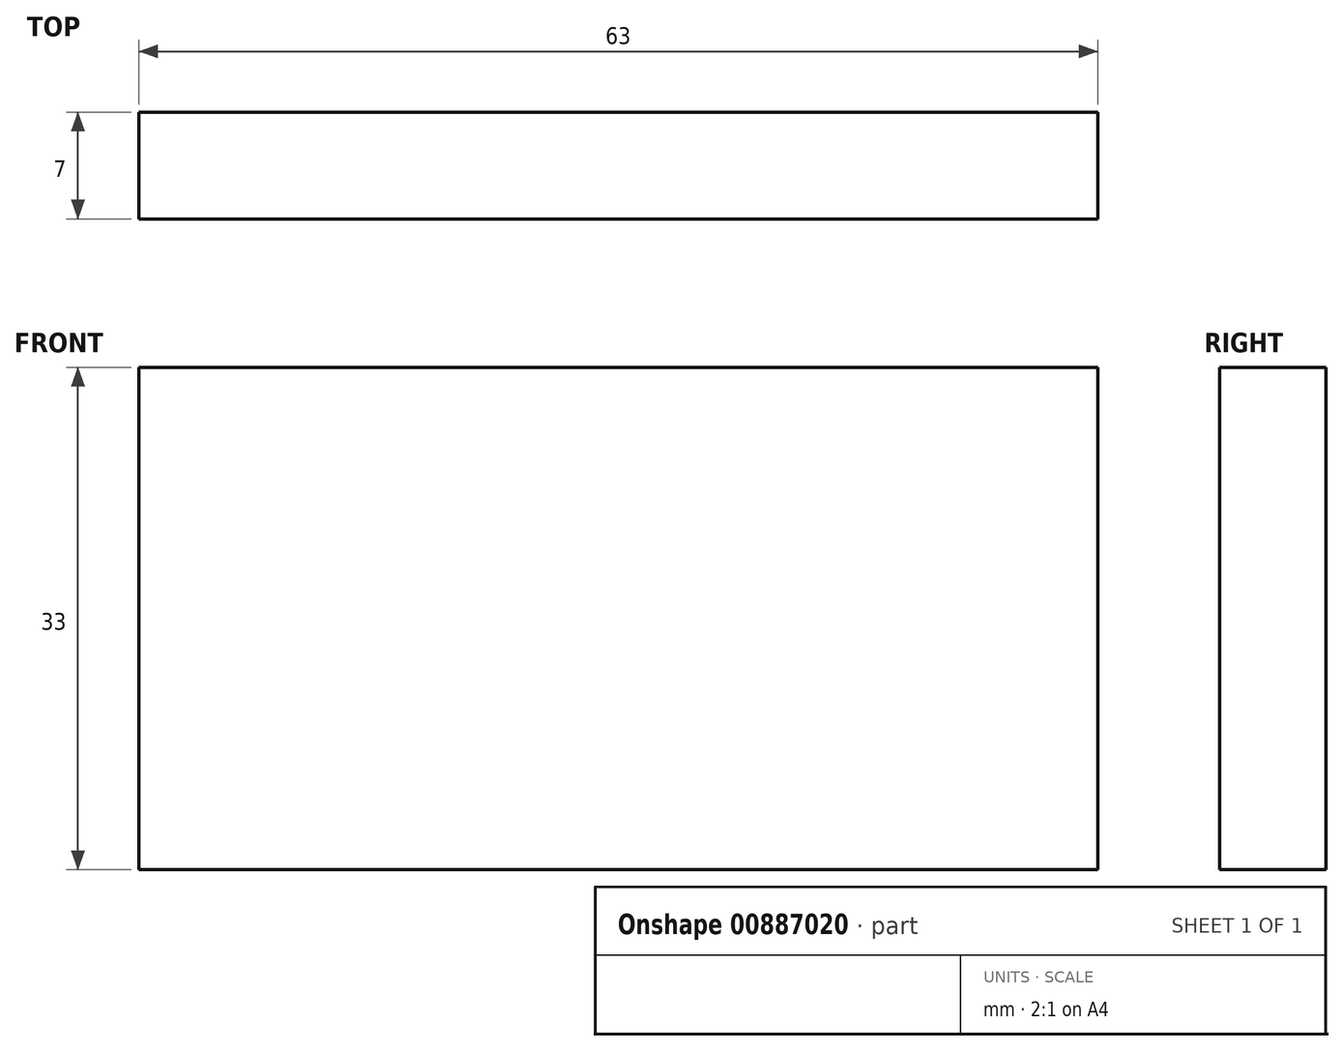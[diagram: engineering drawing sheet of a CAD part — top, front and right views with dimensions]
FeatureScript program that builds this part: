
annotation { "Feature Type Name" : "Feature", "Feature Type Description" : "" }
export const myFeature = defineFeature(function(context is Context, id is Id, definition is map)
    precondition{}
    {
        {
            var Q0;
            Q0=qCreatedBy(makeId("Front.planeOp"),FACE);
            var sketch = newSketch(context, id + "F0", { "sketchPlane" : qUnion([Q0])});
            skLineSegment(sketch, "E0.bottom", {"start": v(-31.5, 16.5) * mm, "end": v(31.5, 16.5) * mm});
            skLineSegment(sketch, "E0.top", {"start": v(-31.5, -16.5) * mm, "end": v(31.5, -16.5) * mm});
            skLineSegment(sketch, "E0.left", {"start": v(-31.5, 16.5) * mm, "end": v(-31.5, -16.5) * mm});
            skLineSegment(sketch, "E0.right", {"start": v(31.5, 16.5) * mm, "end": v(31.5, -16.5) * mm});
            skSolve(sketch);
        }
        {
            var Q0;
            Q0 = qSketchRegion(id + "F0", true);
            extrude(context, id + "F1", {"entities" : qUnion([Q0]), "depth" : 7 * mm, "offsetDistance" : 25 * mm});
        }
    });
